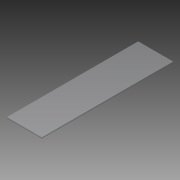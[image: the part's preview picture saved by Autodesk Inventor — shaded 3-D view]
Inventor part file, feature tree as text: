
AUTODESK INVENTOR PART (.ipt)
format: ipt  version: 2014 SP1 (Build 180222100, 222)  size: 69,120 bytes
history: native  units: in
note: dims shown in document units (in); Inventor stores cm internally (conversion verified against a paired STEP export)
features: extrude x1, sketch x1
ambient origin geometry x8: Origin, YZ Plane, XZ Plane, XY Plane, X Axis, Y Axis, Z Axis, Center Point
bodies: Solid1 (feature_tree)
feature tree (2):
  extrude  "Extrusion1"  Depth=7.5in
  sketch  "Sketch1"  dims[d0=2.0in d1=7.5in d2=0.0625in d3=0.0in]
